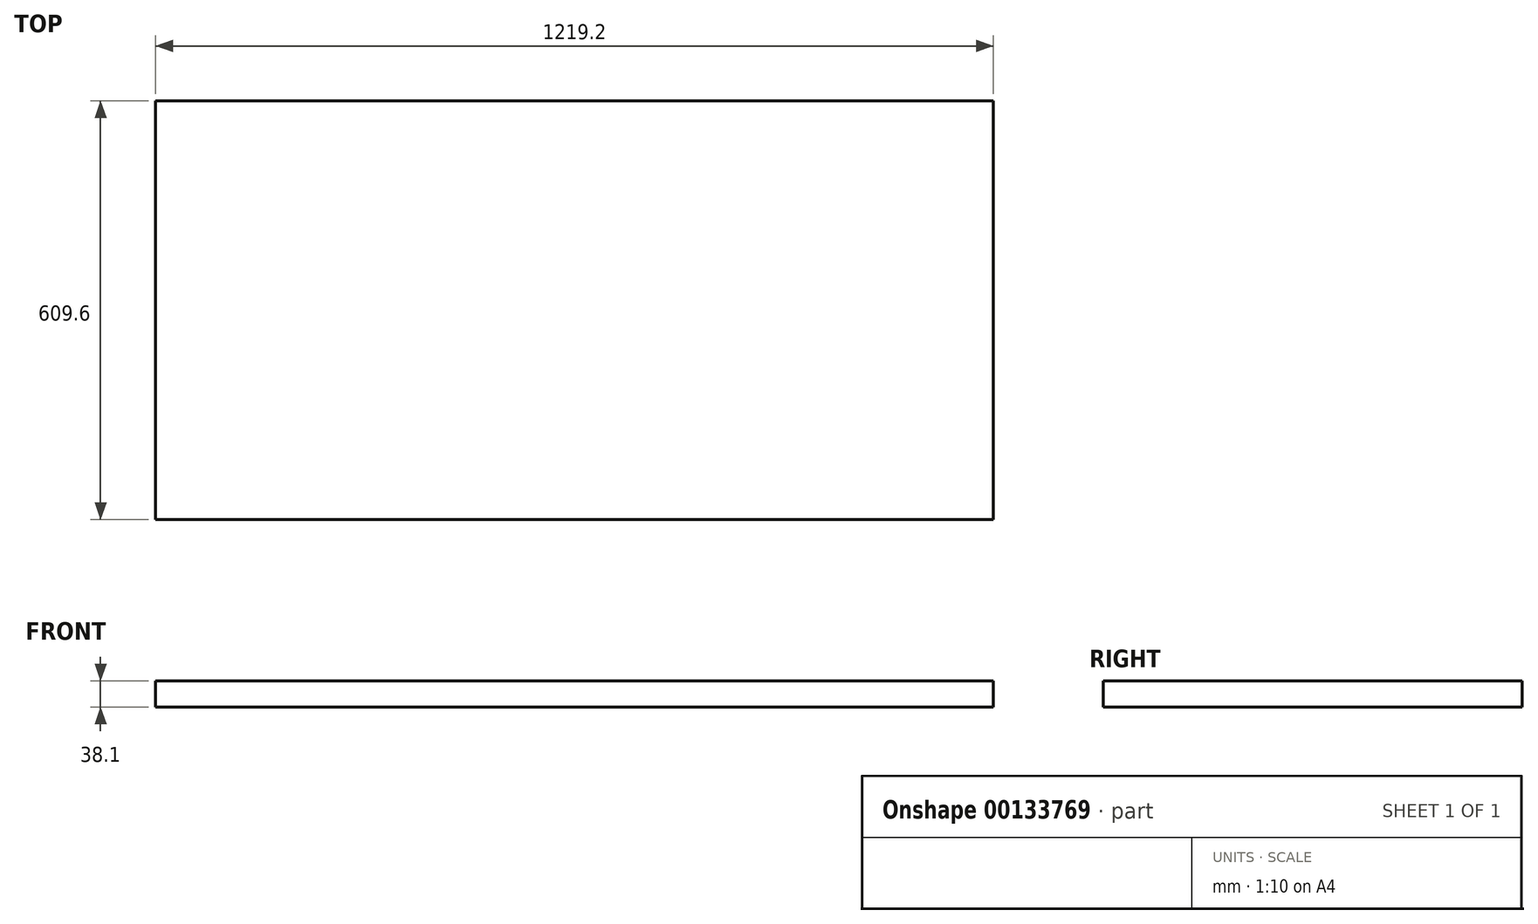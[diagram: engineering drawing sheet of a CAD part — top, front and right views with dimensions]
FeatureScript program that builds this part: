
annotation { "Feature Type Name" : "Feature", "Feature Type Description" : "" }
export const myFeature = defineFeature(function(context is Context, id is Id, definition is map)
    precondition{}
    {
        {
            var Q0;
            Q0=qCreatedBy(makeId("Top.planeOp"),FACE);
            var sketch = newSketch(context, id + "F0", { "sketchPlane" : qUnion([Q0])});
            skLineSegment(sketch, "E0.bottom", {"start": v(609.6, -304.8) * mm, "end": v(-609.6, -304.8) * mm});
            skLineSegment(sketch, "E0.top", {"start": v(609.6, 304.8) * mm, "end": v(-609.6, 304.8) * mm});
            skLineSegment(sketch, "E0.left", {"start": v(609.6, -304.8) * mm, "end": v(609.6, 304.8) * mm});
            skLineSegment(sketch, "E0.right", {"start": v(-609.6, -304.8) * mm, "end": v(-609.6, 304.8) * mm});
            skPoint(sketch, "E0.middle", {"position": v(0, 0) * mm});
            skSolve(sketch);
        }
        {
            var Q0;
            Q0=makeQuery(id+"F0.imprint","IMPRINT",FACE,{"disambiguationData":[TD([[makeQuery(id+"F0.imprint","IMPRINT",EDGE,{"derivedFrom":sQuery(id+"F0.wireOp",EDGE,"E0.bottom")}),-1.0]])]});
            extrude(context, id + "F1", {"entities" : qUnion([Q0]), "depth" : 38.1 * mm});
        }
    });
